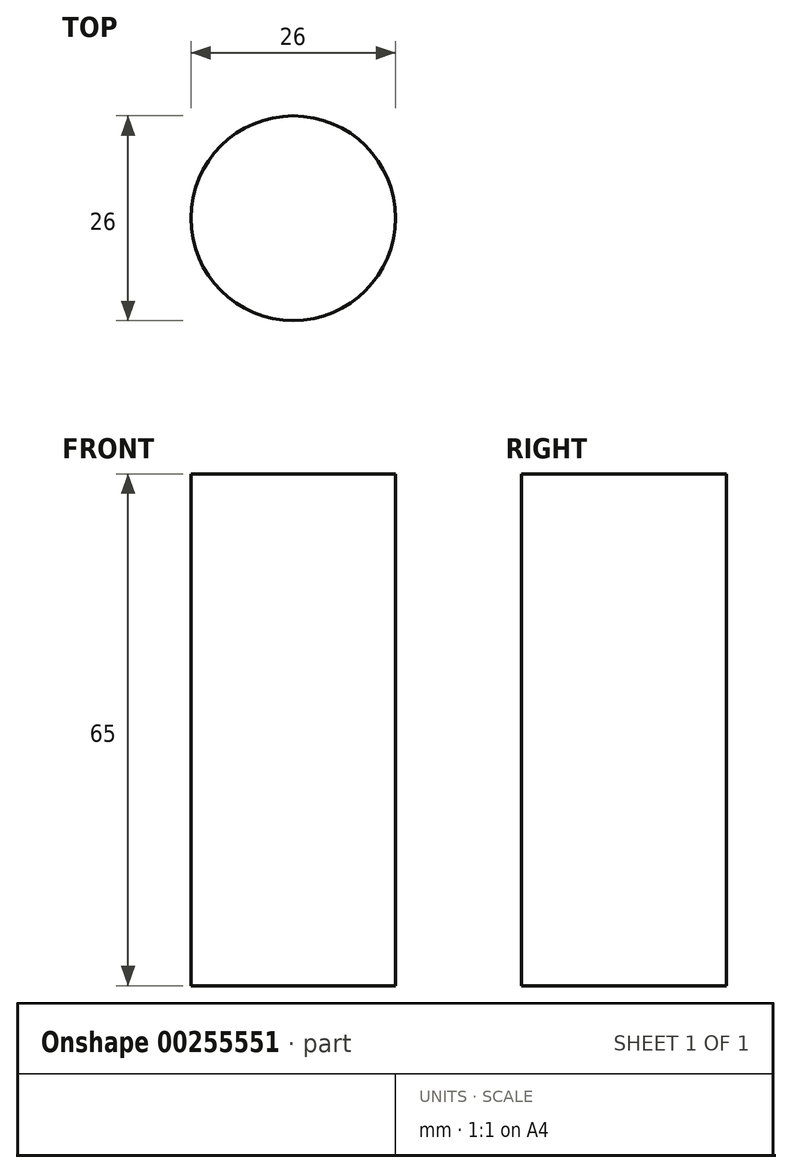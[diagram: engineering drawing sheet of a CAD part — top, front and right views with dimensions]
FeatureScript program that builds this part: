
annotation { "Feature Type Name" : "Feature", "Feature Type Description" : "" }
export const myFeature = defineFeature(function(context is Context, id is Id, definition is map)
    precondition{}
    {
        {
            var Q0;
            Q0=qCreatedBy(makeId("Top.planeOp"),FACE);
            var sketch = newSketch(context, id + "F0", { "sketchPlane" : qUnion([Q0])});
            skCircle(sketch, "E0", {"center": v(0, 0) * mm, "radius": 13 * mm});
            skSolve(sketch);
        }
        {
            var Q0;
            Q0=makeQuery(id+"F0.imprint","IMPRINT",FACE,{"disambiguationData":[TD([[makeQuery(id+"F0.imprint","IMPRINT",EDGE,{"derivedFrom":sQuery(id+"F0.wireOp",EDGE,"E0")}),1.0]])]});
            extrude(context, id + "F1", {"entities" : qUnion([Q0]), "depth" : 65 * mm});
        }
    });
